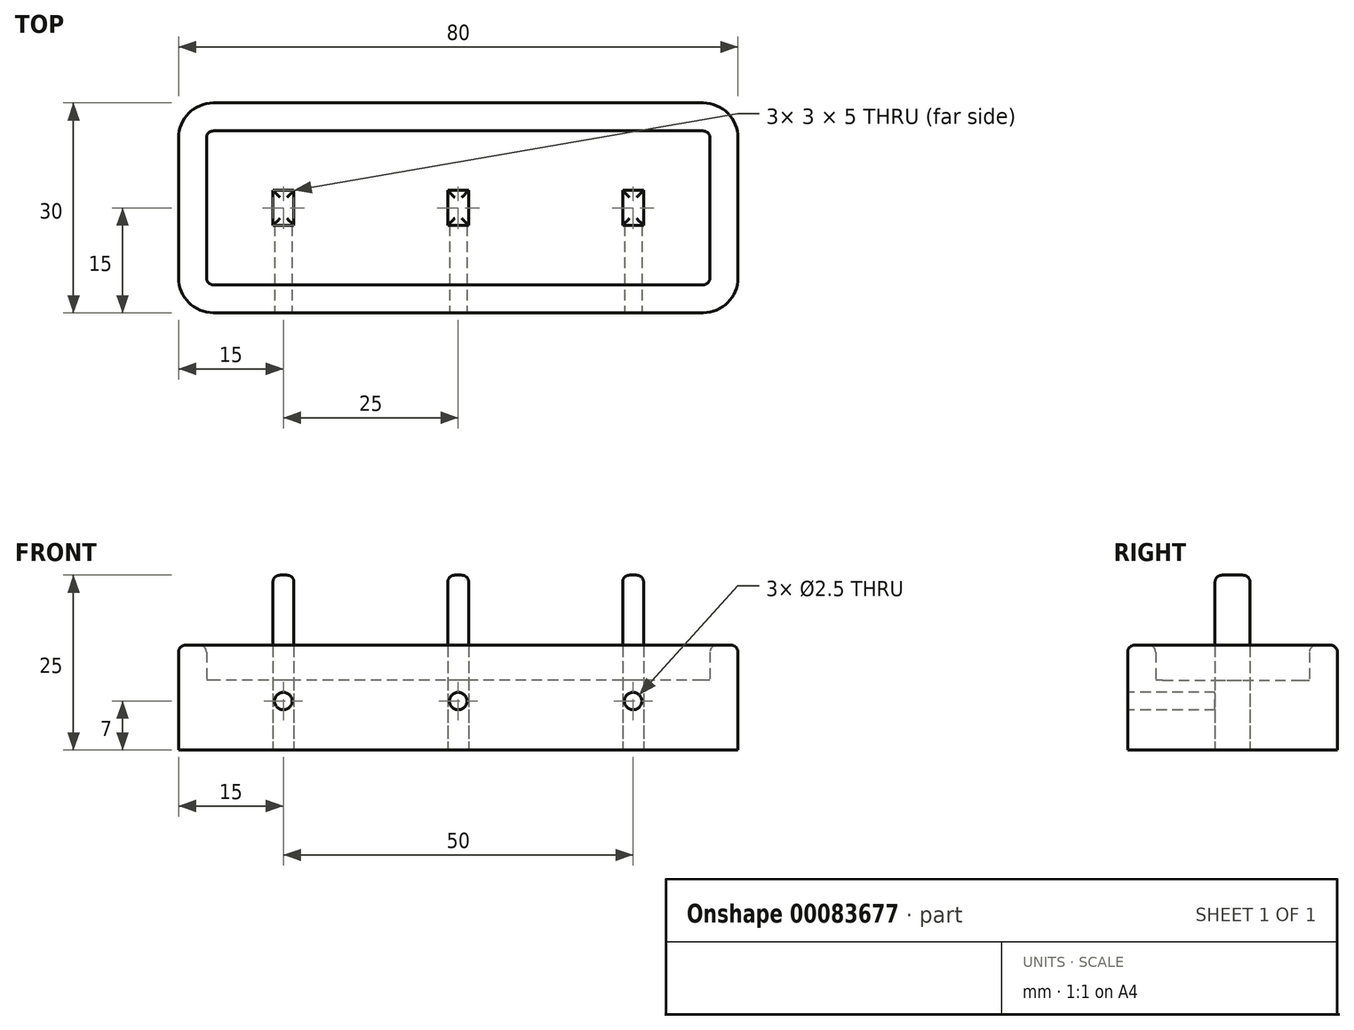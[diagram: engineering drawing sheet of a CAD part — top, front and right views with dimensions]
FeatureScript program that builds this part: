
annotation { "Feature Type Name" : "Feature", "Feature Type Description" : "" }
export const myFeature = defineFeature(function(context is Context, id is Id, definition is map)
    precondition{}
    {
        {
            var Q0;
            Q0=qCreatedBy(makeId("Top.planeOp"),FACE);
            var sketch = newSketch(context, id + "F0", { "sketchPlane" : qUnion([Q0])});
            skLineSegment(sketch, "E0.bottom", {"start": v(35, -15) * mm, "end": v(-35, -15) * mm});
            skLineSegment(sketch, "E0.top", {"start": v(35, 15) * mm, "end": v(-35, 15) * mm});
            skLineSegment(sketch, "E0.left", {"start": v(40, -10) * mm, "end": v(40, 10) * mm});
            skLineSegment(sketch, "E0.right", {"start": v(-40, -10) * mm, "end": v(-40, 10) * mm});
            skPoint(sketch, "E0.middle", {"position": v(0, 0) * mm});
            skLineSegment(sketch, "E1", {"start": v(-40, 0) * mm, "end": v(-25, 0) * mm, "construction": true});
            skLineSegment(sketch, "E2", {"start": v(-25, 0) * mm, "end": v(0, 0) * mm, "construction": true});
            skLineSegment(sketch, "E3", {"start": v(25, 0) * mm, "end": v(40, 0) * mm, "construction": true});
            skLineSegment(sketch, "E4", {"start": v(0, 0) * mm, "end": v(25, 0) * mm, "construction": true});
            skLineSegment(sketch, "E5.bottom", {"start": v(-23.5, -2.5) * mm, "end": v(-26.5, -2.5) * mm});
            skLineSegment(sketch, "E5.top", {"start": v(-23.5, 2.5) * mm, "end": v(-26.5, 2.5) * mm});
            skLineSegment(sketch, "E5.left", {"start": v(-23.5, -2.5) * mm, "end": v(-23.5, 2.5) * mm});
            skLineSegment(sketch, "E5.right", {"start": v(-26.5, -2.5) * mm, "end": v(-26.5, 2.5) * mm});
            skPoint(sketch, "E5.middle", {"position": v(-25, 0) * mm});
            skLineSegment(sketch, "E6.bottom", {"start": v(1.5, -2.5) * mm, "end": v(-1.5, -2.5) * mm});
            skLineSegment(sketch, "E6.top", {"start": v(1.5, 2.5) * mm, "end": v(-1.5, 2.5) * mm});
            skLineSegment(sketch, "E6.left", {"start": v(1.5, -2.5) * mm, "end": v(1.5, 2.5) * mm});
            skLineSegment(sketch, "E6.right", {"start": v(-1.5, -2.5) * mm, "end": v(-1.5, 2.5) * mm});
            skLineSegment(sketch, "E7.bottom", {"start": v(26.5, -2.5) * mm, "end": v(23.5, -2.5) * mm});
            skLineSegment(sketch, "E7.top", {"start": v(26.5, 2.5) * mm, "end": v(23.5, 2.5) * mm});
            skLineSegment(sketch, "E7.left", {"start": v(26.5, -2.5) * mm, "end": v(26.5, 2.5) * mm});
            skLineSegment(sketch, "E7.right", {"start": v(23.5, -2.5) * mm, "end": v(23.5, 2.5) * mm});
            skPoint(sketch, "E7.middle", {"position": v(25, 0) * mm});
            skPoint(sketch, "E8.visualSharp", {"position": v(-40, 15) * mm});
            skArc(sketch, "E8.filletArc", {"start": v(-35, 15) * mm, "mid": v(-38.54, 13.54) * mm, "end": v(-40, 10) * mm});
            skPoint(sketch, "E9.visualSharp", {"position": v(-40, -15) * mm});
            skArc(sketch, "E9.filletArc", {"start": v(-40, -10) * mm, "mid": v(-38.54, -13.54) * mm, "end": v(-35, -15) * mm});
            skPoint(sketch, "E10.visualSharp", {"position": v(40, -15) * mm});
            skArc(sketch, "E10.filletArc", {"start": v(35, -15) * mm, "mid": v(38.54, -13.54) * mm, "end": v(40, -10) * mm});
            skPoint(sketch, "E11.visualSharp", {"position": v(40, 15) * mm});
            skArc(sketch, "E11.filletArc", {"start": v(40, 10) * mm, "mid": v(38.54, 13.54) * mm, "end": v(35, 15) * mm});
            skArc(sketch, "E12.0", {"start": v(36, 10) * mm, "mid": v(35.7, 10.7) * mm, "end": v(35, 11) * mm});
            skLineSegment(sketch, "E12.1", {"start": v(36, -10) * mm, "end": v(36, 10) * mm});
            skLineSegment(sketch, "E12.2", {"start": v(35, 11) * mm, "end": v(-35, 11) * mm});
            skArc(sketch, "E12.3", {"start": v(35, -11) * mm, "mid": v(35.7, -10.7) * mm, "end": v(36, -10) * mm});
            skArc(sketch, "E12.4", {"start": v(-35, 11) * mm, "mid": v(-35.7, 10.7) * mm, "end": v(-36, 10) * mm});
            skLineSegment(sketch, "E12.5", {"start": v(-36, -10) * mm, "end": v(-36, 10) * mm});
            skArc(sketch, "E12.6", {"start": v(-36, -10) * mm, "mid": v(-35.7, -10.7) * mm, "end": v(-35, -11) * mm});
            skLineSegment(sketch, "E12.7", {"start": v(35, -11) * mm, "end": v(-35, -11) * mm});
            skSolve(sketch);
        }
        {
            var Q0;
            Q0=makeQuery(id+"F0.imprint","IMPRINT",FACE,{"disambiguationData":[TD([[makeQuery(id+"F0.imprint","IMPRINT",EDGE,{"derivedFrom":sQuery(id+"F0.wireOp",EDGE,"E5.bottom")}),-1.0]])]});
            var Q1;
            Q1=makeQuery(id+"F0.imprint","IMPRINT",FACE,{"disambiguationData":[TD([[makeQuery(id+"F0.imprint","IMPRINT",EDGE,{"derivedFrom":sQuery(id+"F0.wireOp",EDGE,"E6.bottom")}),-1.0]])]});
            var Q2;
            Q2=makeQuery(id+"F0.imprint","IMPRINT",FACE,{"disambiguationData":[TD([[makeQuery(id+"F0.imprint","IMPRINT",EDGE,{"derivedFrom":sQuery(id+"F0.wireOp",EDGE,"E7.bottom")}),-1.0]])]});
            extrude(context, id + "F1", {"entities" : qUnion([Q0, Q1, Q2]), "depth" : 25 * mm});
        }
        {
            var Q0;
            Q0=makeQuery(id+"F0.imprint","IMPRINT",FACE,{"disambiguationData":[TD([[makeQuery(id+"F0.imprint","IMPRINT",EDGE,{"derivedFrom":sQuery(id+"F0.wireOp",EDGE,"E5.bottom")}),1.0]])]});
            extrude(context, id + "F2", {"entities" : qUnion([Q0]), "depth" : 10 * mm});
        }
        {
            var Q0;
            Q0=makeQuery(id+"F0.imprint","IMPRINT",FACE,{"disambiguationData":[TD([[makeQuery(id+"F0.imprint","IMPRINT",EDGE,{"derivedFrom":sQuery(id+"F0.wireOp",EDGE,"E0.bottom")}),-1.0]])]});
            extrude(context, id + "F3", {"entities" : qUnion([Q0]), "operationType" : NewBodyOperationType.ADD, "depth" : 15 * mm});
        }
        {
            var Q0;
            Q0=makeQuery(id+"F1.opExtrude","CAP_FACE",FACE,{"disambiguationData":[OSD([sQuery(id+"F0.wireOp",EDGE,"E7.bottom"),sQuery(id+"F0.wireOp",EDGE,"E7.top"),sQuery(id+"F0.wireOp",EDGE,"E7.left"),sQuery(id+"F0.wireOp",EDGE,"E7.right")])],"isStart":false});
            var Q1;
            Q1=makeQuery(id+"F1.opExtrude","CAP_FACE",FACE,{"disambiguationData":[OSD([sQuery(id+"F0.wireOp",EDGE,"E6.bottom"),sQuery(id+"F0.wireOp",EDGE,"E6.top"),sQuery(id+"F0.wireOp",EDGE,"E6.left"),sQuery(id+"F0.wireOp",EDGE,"E6.right")])],"isStart":false});
            var Q2;
            Q2=makeQuery(id+"F1.opExtrude","CAP_FACE",FACE,{"disambiguationData":[OSD([sQuery(id+"F0.wireOp",EDGE,"E5.bottom"),sQuery(id+"F0.wireOp",EDGE,"E5.top"),sQuery(id+"F0.wireOp",EDGE,"E5.left"),sQuery(id+"F0.wireOp",EDGE,"E5.right")])],"isStart":false});
            var Q3;
            Q3=makeQuery(id+"F3.opExtrude","CAP_FACE",FACE,{"disambiguationData":[OSD([sQuery(id+"F0.wireOp",EDGE,"E0.bottom"),sQuery(id+"F0.wireOp",EDGE,"E0.top"),sQuery(id+"F0.wireOp",EDGE,"E0.left"),sQuery(id+"F0.wireOp",EDGE,"E0.right"),sQuery(id+"F0.wireOp",EDGE,"E8.filletArc"),sQuery(id+"F0.wireOp",EDGE,"E9.filletArc"),sQuery(id+"F0.wireOp",EDGE,"E10.filletArc"),sQuery(id+"F0.wireOp",EDGE,"E11.filletArc"),sQuery(id+"F0.wireOp",EDGE,"E12.0"),sQuery(id+"F0.wireOp",EDGE,"E12.1"),sQuery(id+"F0.wireOp",EDGE,"E12.2"),sQuery(id+"F0.wireOp",EDGE,"E12.3"),sQuery(id+"F0.wireOp",EDGE,"E12.4"),sQuery(id+"F0.wireOp",EDGE,"E12.5"),sQuery(id+"F0.wireOp",EDGE,"E12.6"),sQuery(id+"F0.wireOp",EDGE,"E12.7")])],"isStart":false});
            fillet(context, id + "F4", {"entities" : qUnion([Q0, Q1, Q2, Q3]), "radius" : 1 * mm, "tangentPropagation" : true, "allowEdgeOverflow" : false});
        }
        {
            var Q0;
            Q0=makeQuery(id+"F3.opExtrude","SWEPT_FACE",FACE,{"disambiguationData":[OSD([sQuery(id+"F0.wireOp",EDGE,"E0.bottom")])]});
            var sketch = newSketch(context, id + "F5", { "sketchPlane" : qUnion([Q0])});
            skLineSegment(sketch, "E13", {"start": v(-25, 0) * mm, "end": v(-25, 14) * mm, "construction": true});
            skLineSegment(sketch, "E14", {"start": v(0, 0) * mm, "end": v(0, 14) * mm, "construction": true});
            skLineSegment(sketch, "E15", {"start": v(25, 0) * mm, "end": v(25, 14) * mm, "construction": true});
            skPoint(sketch, "E16", {"position": v(-25, 7) * mm});
            skPoint(sketch, "E17", {"position": v(0, 7) * mm});
            skPoint(sketch, "E18", {"position": v(25, 7) * mm});
            skSolve(sketch);
        }
        {
            var Q0;
            Q0=sQuery(id+"F5.wireOp",VERTEX,"E16");
            var Q1;
            Q1=sQuery(id+"F5.wireOp",VERTEX,"E17");
            var Q2;
            Q2=sQuery(id+"F5.wireOp",VERTEX,"E18");
            var Q3;
            Q3=makeQuery(id+"F2.opExtrude","SWEPT_BODY",BODY,{"disambiguationData":[OSD([sQuery(id+"F0.wireOp",EDGE,"E5.bottom"),sQuery(id+"F0.wireOp",EDGE,"E5.top"),sQuery(id+"F0.wireOp",EDGE,"E5.left"),sQuery(id+"F0.wireOp",EDGE,"E5.right"),sQuery(id+"F0.wireOp",EDGE,"E6.bottom"),sQuery(id+"F0.wireOp",EDGE,"E6.top"),sQuery(id+"F0.wireOp",EDGE,"E6.left"),sQuery(id+"F0.wireOp",EDGE,"E6.right"),sQuery(id+"F0.wireOp",EDGE,"E7.bottom"),sQuery(id+"F0.wireOp",EDGE,"E7.top"),sQuery(id+"F0.wireOp",EDGE,"E7.left"),sQuery(id+"F0.wireOp",EDGE,"E7.right"),sQuery(id+"F0.wireOp",EDGE,"E12.0"),sQuery(id+"F0.wireOp",EDGE,"E12.1"),sQuery(id+"F0.wireOp",EDGE,"E12.2"),sQuery(id+"F0.wireOp",EDGE,"E12.3"),sQuery(id+"F0.wireOp",EDGE,"E12.4"),sQuery(id+"F0.wireOp",EDGE,"E12.5"),sQuery(id+"F0.wireOp",EDGE,"E12.6"),sQuery(id+"F0.wireOp",EDGE,"E12.7")])]});
            hole(context, id + "F6", {"style" : HoleStyle.SIMPLE, "endStyle" : HoleEndStyle.BLIND, "holeDiameter" : 2.5 * mm, "holeDepth" : 15 * mm, "locations" : qUnion([Q0, Q1, Q2]), "scope" : qUnion([Q3])});
        }
    });
